# Revit family: Hager-Univers-IP44-D161-Cl.II-FWQ-encl-AT-de
name_source: partatom
category: Equipement électrique
units: mm (PartAtom-declared; Revit-internal decimal feet)

## family parameters
Configuration du panneau = Deux colonnes, circuits au sein
Cote de connecteur circulaire = Utiliser le diamètre
Couper avec des vides une fois chargée = Non
Hôte = Face
Partagée = Non
Point de calcul de pièce = Non
Type d'élément = Tableau de raccordement

## types (14) — shared parameters
Commentaires du type = Univers
EF000003 - Montageart = EV000384 - Aufputz
EF000007 - Farbe = EV000202 - weiß
EF000049 - Tiefe = 161 mm  [stored 0.528215 ft]
EF000116 - RAL-Nummer = 9010
EF000118 - Mit Montageplatte = Oui
EF000339 - Art der Abdeckung = EV001012 - Deckel
EF001088 - Anbaumöglichkeit = Oui
EF001131 - Innentiefe = 161 mm  [stored 0.528215 ft]
EF001596 - Werkstoff des Gehäuses = EV000179 - Stahl
EF001613 - Funktionserhalt = EV000494 - ohne
EF003532 - Geeignet für Außengebrauch = Non
EF004293 - Schlagfestigkeit = EV006815 - IK09
EF004464 - Art der Tür = EV002646 - Einzel
EF005474 - Schutzart (IP) = EV006418 - IP44
EF006244 - Transparenter Deckel/Tür = Non
EF006306 - Mit Schloss = Non
EF007800 - Geeignet für Blitzschutz = Non
EF008873 - Nennstrom (In) = 125 A
EF009170 - Materialstärke Gehäuse = 2 mm  [stored 0.00656168 ft]
EF009171 - Materialstärke Tür/Deckel = 2 mm  [stored 0.00656168 ft]
EF009212 - Ausführung Deckel = EV009916 - mit Ausschnitt
EF015940 - Deckel mit Überdruckentlastung = Non
Fabricant = Hager
HG000002 - Mit tür = Oui
HG000003 - Bereich = Univers
HG000006 - Unterputz = Non
HG000023 - Gehäuse mit doppeltem Querschnitt = Non
HG000024 - Höhe des unteren Teils = 800 mm  [stored 2.62467 ft]
HG000026 - Stehend auf dem Boden = Non
zero-valued in all types: EF000218 - Einbautiefe, Elévation par défaut, HG000027 - Sockelhöhe

## per-type parameters (varying)
| type | EF000008 - Breite | EF000040 - Höhe | EF000266 - Anzahl der Reihen | EF000437 - Anzahl der Leitungseinführungen | EF002950 - Breite in Teilungseinheiten | EF004427 - Anzahl der Module | EF009554 - Anzahl der Öffnungen für Flanschplatten | HG000004 - Herstellerreferenz | HG000009 - Doppelflügeligen Tür | HG000010 - Asymmetrische Türen |
| Aufputz IP44 B1050 H1100 T161  - FWQ74N | 1050 mm | 1100 mm | 4 | 16 | 48 | 240 | 8 | FWQ74N | Oui | Non |
| Aufputz IP44 B1050 H500 T161  - FWQ34P | 1050 mm | 500 mm  [stored 1.64042 ft] | 4 | 16 | 48 | 144 | 8 | FWQ34P | Oui | Non |
| Aufputz IP44 B1050 H650 T161  - FWQ44P | 1050 mm | 650 mm | 4 | 16 | 48 | 192 | 8 | FWQ44P | Oui | Non |
| Aufputz IP44 B300 H650 T161  - FWQ41P | 300 mm | 650 mm | 1 | 4 | 12 | 48 | 2 | FWQ41P | Non | Non |
| Aufputz IP44 B550 H1100 T161  - FWQ72N | 550 mm | 1100 mm | 2 | 8 | 24 | 120 | 4 | FWQ72N | Non | Non |
| Aufputz IP44 B550 H500 T161  - FWQ32P | 550 mm | 500 mm  [stored 1.64042 ft] | 8 | 8 | 24 | 96 | 4 | FWQ32P | Non | Non |
| Aufputz IP44 B550 H650 T161  - FWQ42P | 550 mm | 650 mm | 2 | 8 | 24 | 96 | 4 | FWQ42P | Non | Non |
| Aufputz IP44 B550 H800 T161  - FWQ52N | 550 mm | 800 mm  [stored 2.62467 ft] | 2 | 8 | 24 | 72 | 4 | FWQ52N | Non | Non |
| Aufputz IP44 B550 H950 T161  - FWQ62N | 550 mm | 950 mm  [stored 3.1168 ft] | 2 | 8 | 24 | 96 | 4 | FWQ62N | Non | Non |
| Aufputz IP44 B800 H1100 T161  - FWQ73N | 800 mm  [stored 2.62467 ft] | 1100 mm | 3 | 12 | 36 | 180 | 6 | FWQ73N | Oui | Oui |
| Aufputz IP44 B800 H500 T161  - FWQ33P | 800 mm  [stored 2.62467 ft] | 500 mm  [stored 1.64042 ft] | 3 | 12 | 36 | 108 | 6 | FWQ33P | Oui | Oui |
| Aufputz IP44 B800 H650 T161  - FWQ43P | 800 mm  [stored 2.62467 ft] | 650 mm | 3 | 12 | 36 | 144 | 6 | FWQ43P | Oui | Oui |
| Aufputz IP44 B800 H800 T161  - FWQ53N | 800 mm  [stored 2.62467 ft] | 800 mm  [stored 2.62467 ft] | 3 | 12 | 36 | 108 | 6 | FWQ53N | Oui | Oui |
| Aufputz IP44 B800 H950 T161  - FWQ63N | 800 mm  [stored 2.62467 ft] | 950 mm  [stored 3.1168 ft] | 3 | 12 | 36 | 144 | 6 | FWQ63N | Oui | Oui |

note: [stored X ft] marks values corroborated as IEEE doubles in the binary element streams (Revit-internal decimal feet)

## geometry (parser evidence)
native form markers: Sweep x10
no freeform markers — native parametric forms only
